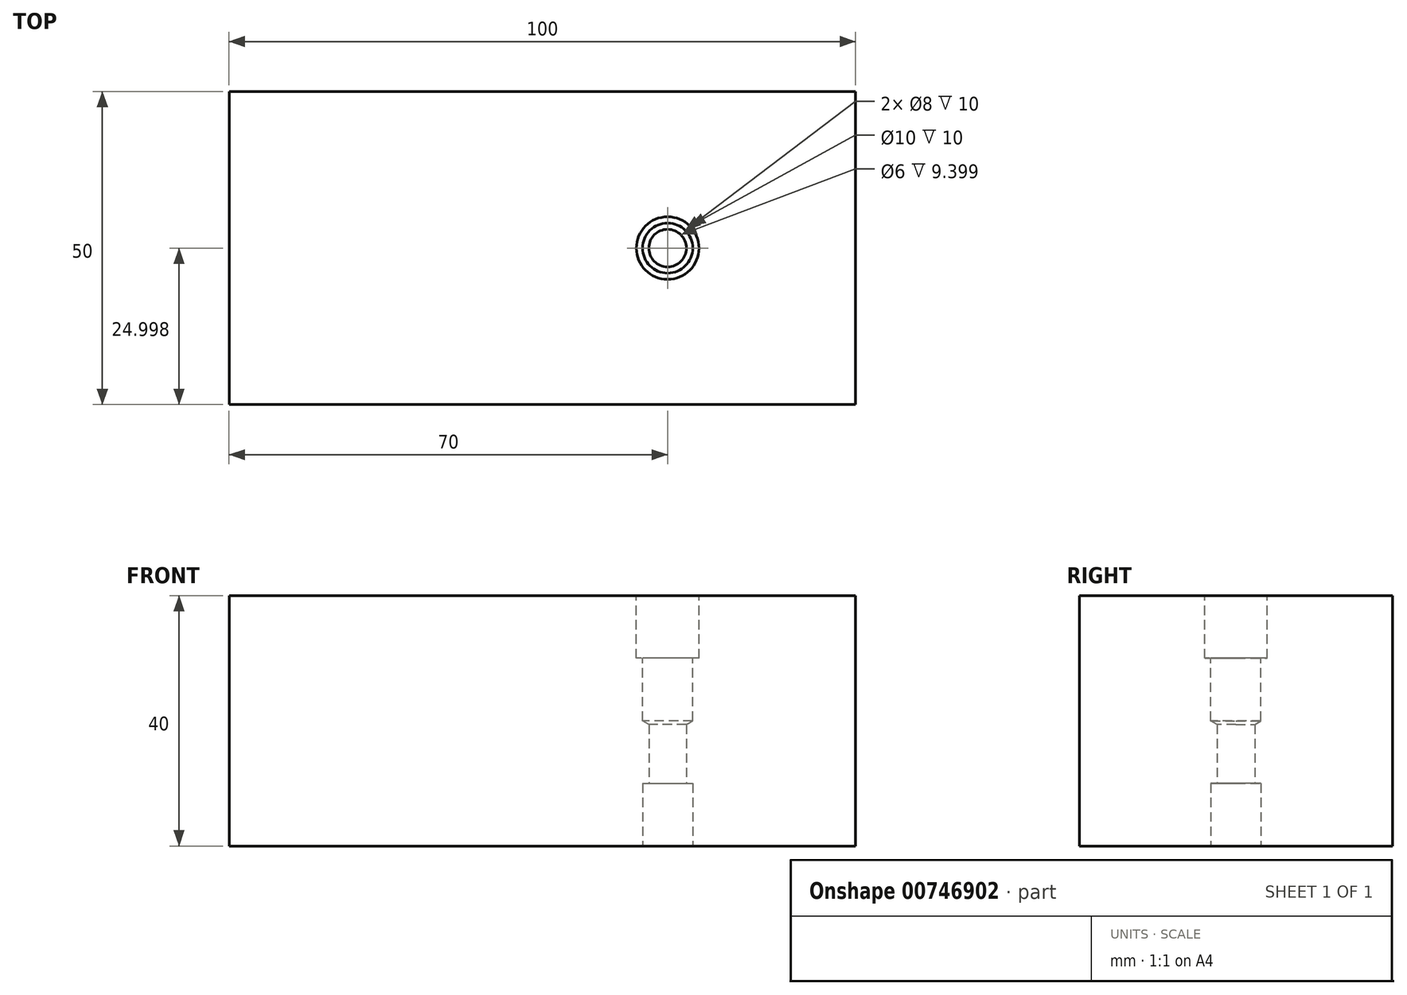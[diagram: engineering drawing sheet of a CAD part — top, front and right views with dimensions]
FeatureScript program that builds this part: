
annotation { "Feature Type Name" : "Feature", "Feature Type Description" : "" }
export const myFeature = defineFeature(function(context is Context, id is Id, definition is map)
    precondition{}
    {
        {
            var Q0;
            Q0=qCreatedBy(makeId("Top.planeOp"),FACE);
            var sketch = newSketch(context, id + "F0", { "sketchPlane" : qUnion([Q0])});
            skLineSegment(sketch, "E0.bottom", {"start": v(-44.64, 16.95) * mm, "end": v(55.36, 16.95) * mm});
            skLineSegment(sketch, "E0.top", {"start": v(-44.64, -33.05) * mm, "end": v(55.36, -33.05) * mm});
            skLineSegment(sketch, "E0.left", {"start": v(-44.64, 16.95) * mm, "end": v(-44.64, -33.05) * mm});
            skLineSegment(sketch, "E0.right", {"start": v(55.36, 16.95) * mm, "end": v(55.36, -33.05) * mm});
            skSolve(sketch);
        }
        {
            var Q0;
            Q0=qSketchRegion(id+"F0",true);
            extrude(context, id + "F1", {"entities" : qUnion([Q0]), "depth" : 40 * mm, "offsetDistance" : 25 * mm});
        }
        {
            var Q0;
            Q0=makeQuery(id+"F1.opExtrude","CAP_FACE",FACE,{"disambiguationData":[OSD([sQuery(id+"F0.wireOp",EDGE,"E0.bottom"),sQuery(id+"F0.wireOp",EDGE,"E0.top"),sQuery(id+"F0.wireOp",EDGE,"E0.left"),sQuery(id+"F0.wireOp",EDGE,"E0.right")])],"isStart":false});
            var sketch = newSketch(context, id + "F2", { "sketchPlane" : qUnion([Q0])});
            skPoint(sketch, "E1", {"position": v(25.36, -8.05) * mm});
            skSolve(sketch);
        }
        {
            var Q0;
            Q0=sQuery(id+"F2.wireOp",VERTEX,"E1");
            var Q1;
            Q1=makeQuery(id+"F1.opExtrude","SWEPT_BODY",BODY,{"disambiguationData":[OSD([sQuery(id+"F0.wireOp",EDGE,"E0.bottom"),sQuery(id+"F0.wireOp",EDGE,"E0.top"),sQuery(id+"F0.wireOp",EDGE,"E0.left"),sQuery(id+"F0.wireOp",EDGE,"E0.right")])]});
            hole(context, id + "F3", {"style" : HoleStyle.C_BORE, "endStyle" : HoleEndStyle.BLIND, "holeDiameter" : 8 * mm, "cBoreDiameter" : 10 * mm, "cBoreDepth" : 10 * mm, "majorDiameter" : 5 * mm, "holeDepth" : 20 * mm, "isTappedThrough" : true, "tappedDepth" : 11.5 * mm, "tapClearance" : 3, "locations" : qUnion([Q0]), "scope" : qUnion([Q1])});
        }
        {
            var Q0;
            Q0=qCreatedBy(makeId("Top.planeOp"),FACE);
            var sketch = newSketch(context, id + "F4", { "sketchPlane" : qUnion([Q0])});
            skPoint(sketch, "E2", {"position": v(25.36, -8.05) * mm});
            skSolve(sketch);
        }
        {
            var Q0;
            Q0=sQuery(id+"F4.wireOp",VERTEX,"E2");
            var Q1;
            Q1=makeQuery(id+"F1.opExtrude","SWEPT_BODY",BODY,{"disambiguationData":[OSD([sQuery(id+"F0.wireOp",EDGE,"E0.bottom"),sQuery(id+"F0.wireOp",EDGE,"E0.top"),sQuery(id+"F0.wireOp",EDGE,"E0.left"),sQuery(id+"F0.wireOp",EDGE,"E0.right")])]});
            hole(context, id + "F5", {"style" : HoleStyle.C_BORE, "endStyle" : HoleEndStyle.BLIND, "oppositeDirection" : true, "holeDiameter" : 6 * mm, "cBoreDiameter" : 8 * mm, "cBoreDepth" : 10 * mm, "majorDiameter" : 5 * mm, "holeDepth" : 20 * mm, "isTappedThrough" : true, "tappedDepth" : 11.5 * mm, "tapClearance" : 3, "locations" : qUnion([Q0]), "scope" : qUnion([Q1])});
        }
    });
